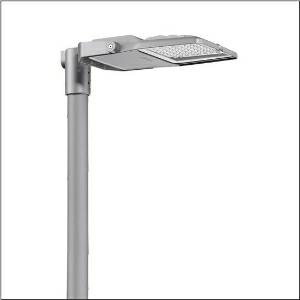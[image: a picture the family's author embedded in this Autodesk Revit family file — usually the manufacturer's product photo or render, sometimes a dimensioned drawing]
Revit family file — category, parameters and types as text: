
# Revit family: floodlight_fl_21_iq_mini___pl64_5xa7772b2e3a_76f3
name_source: partatom
category: Lighting Fixtures
units: mm (PartAtom-declared; Revit-internal decimal feet)

## family parameters
Cut with Voids When Loaded = No
Host = Face
Light Source = No
Part Type = Normal
Room Calculation Point = No
Round Connector Dimension = Use Diameter
Shared = No

## types (1)
- --- (1 x LED, 6020 lm, 45.5 W, 3000K)
    Apparent Load = 46 VA
    CIE Flux Codes = 28 80 98 100 100
    Color Rendering = 70
    Color Temperature = 3000K
    Default Elevation = 1800 mm
    Description = Floodlight FL 21 iQ mini, floodlight, primary light control with lens, of PMMA, primary optical cover: protective disc, of toughened safety glass, transparent, light distribution: PL64, light emission: direct distribution, installation type: surface-mounted, LED, High Power LED, rated luminous flux: 6.020lm, luminous efficacy: 132lm/W, light colour: 730, colour temperature: 3000K, control gear: iQ Street-Remote/DALI, control: Auto-Match, Temp-Guard, Night-Set, Smart-Wire, Desk-Remote (wireless, voltage-free reading and setting of iQ features in the workshop via application-optimized NFC function/RFID function), optimised constant luminous flux control (CLO 2.0), Light-Fading, Lumen-Switch, with terminal, 6-pole, mains connection: 220..240V, AC, 50/60Hz, start of lifetime: 46W, end of service life: 48W, reduction: 22W, luminaire housing, of diecast aluminium, powder-coated, Siteco® metallic grey (DB 702S), corrosivity category C5 mid according to DIN EN ISO 12944, suitable for swimming pools, chlorine-resistant, sealing non-destructively replaceable, please order mast flange separately, mast bracket, of steel, galvanised, powder-coated, protection rating (complete): IP66, insulation class (complete): insulation class II (safety insulation), certification: CE, ENEC, VDE, protection symbol: D, impact resistance: IK08, permissible operating ambient temperature: -40..+40°C, permissible operating ambient temperature for outdoor applications: -40..+50°C, standard: DIN EN 12944, LABS conformity tested according to VDMA 24364:2018-05, packaging unit: 1 piece

Light Distribution: PL64
    Height = 70 mm
    Lamp = 1 x LED
    Lamp Light Flux = 6020 lm
    Lamp Power = 45.5 W
    Lamp count = 1
    Length = 485 mm
    Luminous efficacy = 132 lm/W
    Manufacturer = Siteco
    ModVariant = No
    Model = 5XA7772B2E3A
    Number of Poles = 1
    OnlyDefault = Yes
    Power Factor = 1
    Product Name = Floodlight FL 21 iQ mini | PL64
    Product group = floodlight | pylon annexe
    ProductGroupID = 6201
    Protection Class = Protection class II
    Protection Degree = IP 66
    RLX_Detail_Level = 1
    RLX_Emergency_Light_Flux = 0 lm
    RLX_Emergency_Type = 0
    RLX_Emergency_Type_DB = No
    RlxData = <blob elided: 101329 chars, md5=32f4192e>
    Socket = socket
    Standby Power = 0 W
    System Light Flux = 6020 lm
    System Power = 46 W
    Type Comments = factory setting: luminous flux: 100 % | dim-lin: 254 | 463 mA
    Type Image = l_1007125.jpg
    URL = http://relux.com
    VarID = @adj_188367
    Voltage = 0 V
    Weight = 0.00 kg
    Width = 337 mm

## geometry (parser evidence)
native form markers: Blend x4, Sweep x11
no freeform markers — native parametric forms only
